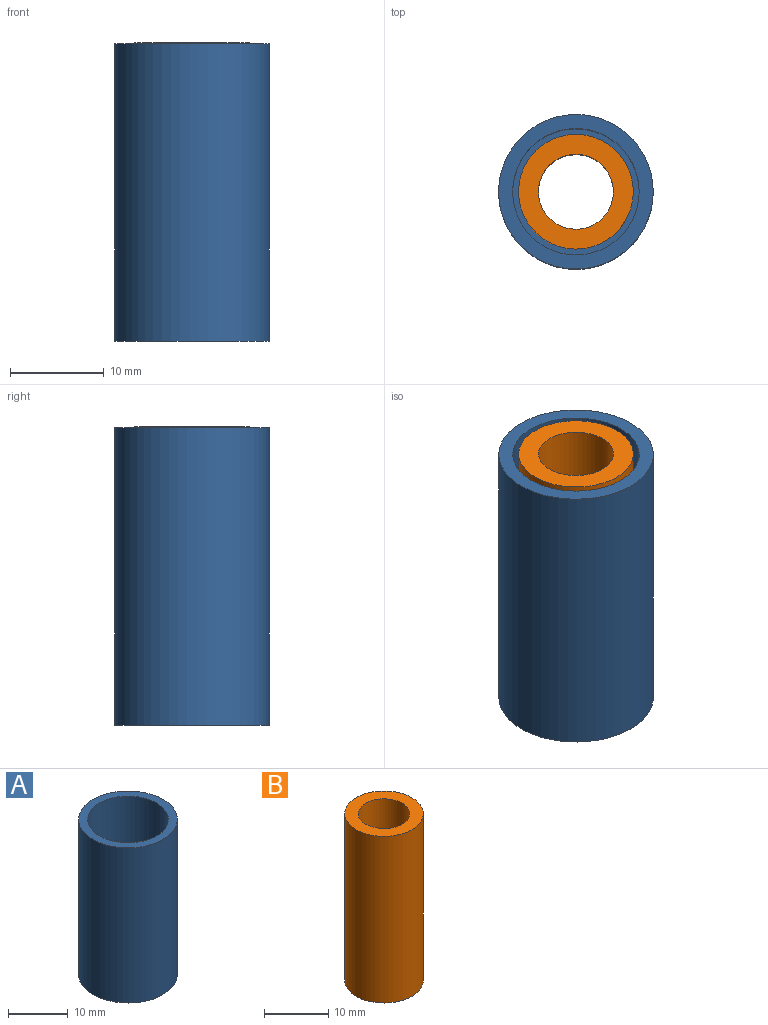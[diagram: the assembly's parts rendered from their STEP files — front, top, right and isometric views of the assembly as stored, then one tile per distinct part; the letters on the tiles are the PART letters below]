
ASSEMBLY  parts=2 mates=1
PART A: 6 faces, bbox 16.5x16.5x31.8 mm
  f0: cylinder r=6.75mm len=29.75mm, axis (0,0,-1), area 1261.7mm2, adj f2,f4
  f1: cylinder r=8.25mm len=31.75mm, axis (0,0,-1), area 1645.8mm2, adj f2,f3
  f2: plane 16.5x16.5mm, normal (0,0,1), area 70.7mm2, adj f0,f1
  f3: plane 16.5x16.5mm, normal (0,0,-1), area 135.3mm2, adj f1,f5
  f4: plane 13.5x13.5mm, normal (0,0,1), area 64.6mm2, adj f0,f5
  f5: cylinder r=5mm len=10mm, axis (0,0,-1), area 62.8mm2, adj f3,f4
PART B: 4 faces, bbox 12.3x12.3x31.8 mm
  f0: cylinder r=6.12mm len=31.75mm, axis (0,0,-1), area 1221.9mm2, adj f1,f2
  f1: plane 12.25x12.25mm, normal (0,0,1), area 67.6mm2, adj f0,f3
  f2: plane 12.25x12.25mm, normal (0,0,-1), area 67.6mm2, adj f0,f3
  f3: cylinder r=4mm len=31.75mm, axis (0,0,1), area 798mm2, adj f1,f2
PLACE A t=(-7.98,2.33,-2.92)mm
PLACE B t=(-7.98,2.33,-2.83)mm
MATE cylindrical B.f0 <-> A.f0  axis (0,0,-1) through (-7.98,2.33,-2.83)mm
